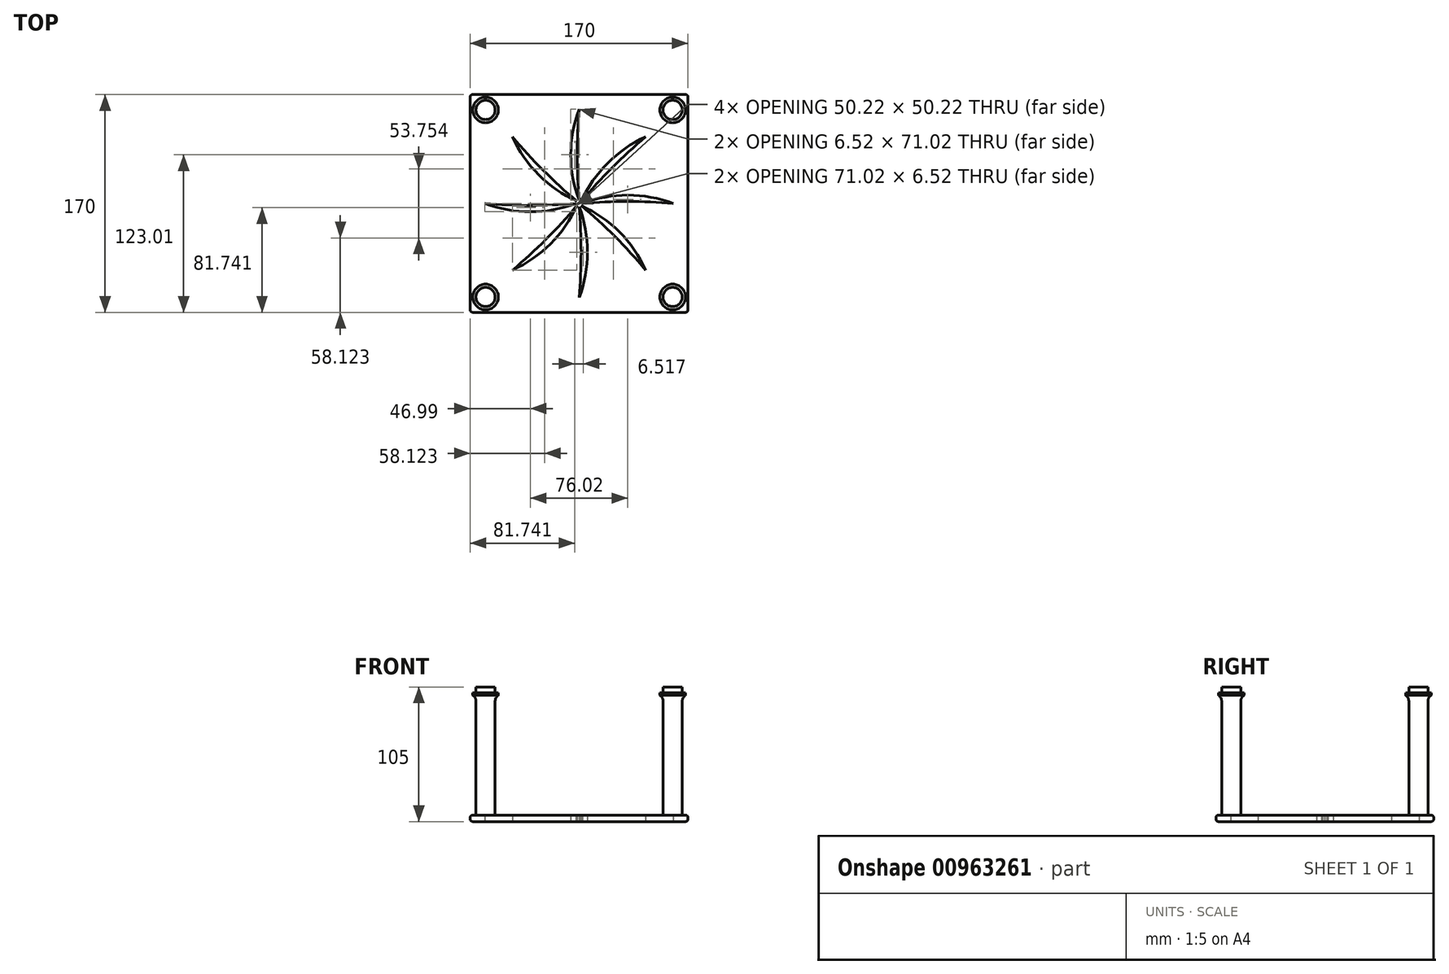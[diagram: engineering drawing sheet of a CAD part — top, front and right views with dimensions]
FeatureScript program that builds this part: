
annotation { "Feature Type Name" : "Feature", "Feature Type Description" : "" }
export const myFeature = defineFeature(function(context is Context, id is Id, definition is map)
    precondition{}
    {
        {
            var Q0;
            Q0=qCreatedBy(makeId("Top.planeOp"),FACE);
            var sketch = newSketch(context, id + "F0", { "sketchPlane" : qUnion([Q0])});
            skLineSegment(sketch, "E0.bottom", {"start": v(85, -85) * mm, "end": v(-85, -85) * mm});
            skLineSegment(sketch, "E0.top", {"start": v(85, 85) * mm, "end": v(-85, 85) * mm});
            skLineSegment(sketch, "E0.left", {"start": v(85, -85) * mm, "end": v(85, 85) * mm});
            skLineSegment(sketch, "E0.right", {"start": v(-85, -85) * mm, "end": v(-85, 85) * mm});
            skPoint(sketch, "E0.middle", {"position": v(0, 0) * mm});
            skSolve(sketch);
        }
        {
            var Q0;
            Q0 = qSketchRegion(id + "F0", true);
            extrude(context, id + "F1", {"entities" : qUnion([Q0]), "depth" : 5 * mm, "offsetDistance" : 25 * mm});
        }
        {
            var Q0;
            Q0=makeQuery(id+"F1.opExtrude","CAP_EDGE",EDGE,{"disambiguationData":[OSD([sQuery(id+"F0.wireOp",EDGE,"E0.bottom")])],"isStart":false});
            var Q1;
            Q1=makeQuery(id+"F1.opExtrude","CAP_EDGE",EDGE,{"disambiguationData":[OSD([sQuery(id+"F0.wireOp",EDGE,"E0.top")])],"isStart":true});
            var Q2;
            Q2=makeQuery(id+"F1.opExtrude","CAP_EDGE",EDGE,{"disambiguationData":[OSD([sQuery(id+"F0.wireOp",EDGE,"E0.top")])],"isStart":false});
            var Q3;
            Q3=makeQuery(id+"F1.opExtrude","CAP_EDGE",EDGE,{"disambiguationData":[OSD([sQuery(id+"F0.wireOp",EDGE,"E0.left")])],"isStart":false});
            var Q4;
            Q4=makeQuery(id+"F1.opExtrude","CAP_EDGE",EDGE,{"disambiguationData":[OSD([sQuery(id+"F0.wireOp",EDGE,"E0.right")])],"isStart":true});
            var Q5;
            Q5=makeQuery(id+"F1.opExtrude","CAP_EDGE",EDGE,{"disambiguationData":[OSD([sQuery(id+"F0.wireOp",EDGE,"E0.right")])],"isStart":false});
            var Q6;
            Q6=makeQuery(id+"F1.opExtrude","SWEPT_EDGE",EDGE,{"disambiguationData":[OSD([sQuery(id+"F0.wireOp",EDGE,"E0.bottom"),sQuery(id+"F0.wireOp",EDGE,"E0.left")])]});
            var Q7;
            Q7=makeQuery(id+"F1.opExtrude","SWEPT_EDGE",EDGE,{"disambiguationData":[OSD([sQuery(id+"F0.wireOp",EDGE,"E0.bottom"),sQuery(id+"F0.wireOp",EDGE,"E0.right")])]});
            var Q8;
            Q8=makeQuery(id+"F1.opExtrude","SWEPT_EDGE",EDGE,{"disambiguationData":[OSD([sQuery(id+"F0.wireOp",EDGE,"E0.top"),sQuery(id+"F0.wireOp",EDGE,"E0.left")])]});
            var Q9;
            Q9=makeQuery(id+"F1.opExtrude","SWEPT_EDGE",EDGE,{"disambiguationData":[OSD([sQuery(id+"F0.wireOp",EDGE,"E0.top"),sQuery(id+"F0.wireOp",EDGE,"E0.right")])]});
            var Q10;
            Q10=makeQuery(id+"F1.opExtrude","CAP_EDGE",EDGE,{"disambiguationData":[OSD([sQuery(id+"F0.wireOp",EDGE,"E0.bottom")])],"isStart":true});
            var Q11;
            Q11=makeQuery(id+"F1.opExtrude","CAP_EDGE",EDGE,{"disambiguationData":[OSD([sQuery(id+"F0.wireOp",EDGE,"E0.left")])],"isStart":true});
            fillet(context, id + "F2", {"entities" : qUnion([Q0, Q1, Q2, Q3, Q4, Q5, Q6, Q7, Q8, Q9, Q10, Q11]), "radius" : 2 * mm, "tangentPropagation" : true, "allowEdgeOverflow" : false});
        }
        {
            var Q0;
            Q0=makeQuery(id+"F1.opExtrude","CAP_FACE",FACE,{"disambiguationData":[OSD([sQuery(id+"F0.wireOp",EDGE,"E0.bottom"),sQuery(id+"F0.wireOp",EDGE,"E0.top"),sQuery(id+"F0.wireOp",EDGE,"E0.left"),sQuery(id+"F0.wireOp",EDGE,"E0.right")])],"isStart":false});
            var sketch = newSketch(context, id + "F3", { "sketchPlane" : qUnion([Q0])});
            skLineSegment(sketch, "E1", {"start": v(-83, 83) * mm, "end": v(-83, 73) * mm, "construction": true});
            skLineSegment(sketch, "E2", {"start": v(-83, 73) * mm, "end": v(-73, 73) * mm, "construction": true});
            skCircle(sketch, "E3", {"center": v(-73, 73) * mm, "radius": 7.5 * mm});
            skLineSegment(sketch, "E4", {"start": v(83, 83) * mm, "end": v(83, 73) * mm, "construction": true});
            skLineSegment(sketch, "E5", {"start": v(83, 73) * mm, "end": v(73, 73) * mm, "construction": true});
            skCircle(sketch, "E6", {"center": v(73, 73) * mm, "radius": 7.5 * mm});
            skLineSegment(sketch, "E7", {"start": v(83, -83) * mm, "end": v(83, -73) * mm, "construction": true});
            skLineSegment(sketch, "E8", {"start": v(83, -73) * mm, "end": v(73, -73) * mm, "construction": true});
            skCircle(sketch, "E9", {"center": v(73, -73) * mm, "radius": 7.5 * mm});
            skLineSegment(sketch, "E10", {"start": v(-83, -83) * mm, "end": v(-73, -83) * mm, "construction": true});
            skLineSegment(sketch, "E11", {"start": v(-73, -83) * mm, "end": v(-73, -73) * mm, "construction": true});
            skCircle(sketch, "E12", {"center": v(-73, -73) * mm, "radius": 7.5 * mm});
            skSolve(sketch);
        }
        {
            var Q0;
            Q0 = qSketchRegion(id + "F3", true);
            extrude(context, id + "F4", {"entities" : qUnion([Q0]), "operationType" : NewBodyOperationType.ADD, "depth" : 95.5 * mm, "offsetDistance" : 25 * mm});
        }
        {
            var Q0;
            Q0=makeQuery(id+"F4.opExtrude","CAP_FACE",FACE,{"disambiguationData":[OSD([sQuery(id+"F3.wireOp",EDGE,"E3")])],"isStart":false});
            var sketch = newSketch(context, id + "F5", { "sketchPlane" : qUnion([Q0])});
            skCircle(sketch, "E13", {"center": v(-73, 73) * mm, "radius": 10 * mm});
            skSolve(sketch);
        }
        {
            var Q0;
            Q0=makeQuery(id+"F4.opExtrude","CAP_FACE",FACE,{"disambiguationData":[OSD([sQuery(id+"F3.wireOp",EDGE,"E6")])],"isStart":false});
            var sketch = newSketch(context, id + "F6", { "sketchPlane" : qUnion([Q0])});
            skCircle(sketch, "E14", {"center": v(73, 73) * mm, "radius": 10 * mm});
            skSolve(sketch);
        }
        {
            var Q0;
            Q0=makeQuery(id+"F4.opExtrude","CAP_FACE",FACE,{"disambiguationData":[OSD([sQuery(id+"F3.wireOp",EDGE,"E9")])],"isStart":false});
            var sketch = newSketch(context, id + "F7", { "sketchPlane" : qUnion([Q0])});
            skCircle(sketch, "E15", {"center": v(73, -73) * mm, "radius": 10 * mm});
            skSolve(sketch);
        }
        {
            var Q0;
            Q0=makeQuery(id+"F4.opExtrude","CAP_FACE",FACE,{"disambiguationData":[OSD([sQuery(id+"F3.wireOp",EDGE,"E12")])],"isStart":false});
            var sketch = newSketch(context, id + "F8", { "sketchPlane" : qUnion([Q0])});
            skCircle(sketch, "E16", {"center": v(-73, -73) * mm, "radius": 10 * mm});
            skSolve(sketch);
        }
        {
            var Q0;
            Q0=makeQuery(id+"F5.imprint","IMPRINT",FACE,{"disambiguationData":[TD([[makeQuery(id+"F5.imprint","IMPRINT",EDGE,{"derivedFrom":makeQuery(id+"F4.opExtrude","CAP_EDGE",EDGE,{"disambiguationData":[OSD([sQuery(id+"F3.wireOp",EDGE,"E3")])],"isStart":false})}),1.0]])]});
            var Q1;
            Q1=makeQuery(id+"F6.imprint","IMPRINT",FACE,{"disambiguationData":[TD([[makeQuery(id+"F6.imprint","IMPRINT",EDGE,{"derivedFrom":makeQuery(id+"F4.opExtrude","CAP_EDGE",EDGE,{"disambiguationData":[OSD([sQuery(id+"F3.wireOp",EDGE,"E6")])],"isStart":false})}),1.0]])]});
            var Q2;
            Q2=makeQuery(id+"F7.imprint","IMPRINT",FACE,{"disambiguationData":[TD([[makeQuery(id+"F7.imprint","IMPRINT",EDGE,{"derivedFrom":makeQuery(id+"F4.opExtrude","CAP_EDGE",EDGE,{"disambiguationData":[OSD([sQuery(id+"F3.wireOp",EDGE,"E9")])],"isStart":false})}),1.0]])]});
            var Q3;
            Q3=makeQuery(id+"F8.imprint","IMPRINT",FACE,{"disambiguationData":[TD([[makeQuery(id+"F8.imprint","IMPRINT",EDGE,{"derivedFrom":makeQuery(id+"F4.opExtrude","CAP_EDGE",EDGE,{"disambiguationData":[OSD([sQuery(id+"F3.wireOp",EDGE,"E12")])],"isStart":false})}),1.0]])]});
            extrude(context, id + "F9", {"entities" : qUnion([Q0, Q1, Q2, Q3]), "operationType" : NewBodyOperationType.ADD, "depth" : 4.5 * mm, "offsetDistance" : 25 * mm});
        }
        {
            var Q0;
            Q0=makeQuery(id+"F5.imprint","IMPRINT",FACE,{"disambiguationData":[TD([[makeQuery(id+"F5.imprint","IMPRINT",EDGE,{"derivedFrom":sQuery(id+"F5.wireOp",EDGE,"E13")}),1.0]])]});
            var Q1;
            Q1=makeQuery(id+"F6.imprint","IMPRINT",FACE,{"disambiguationData":[TD([[makeQuery(id+"F6.imprint","IMPRINT",EDGE,{"derivedFrom":sQuery(id+"F6.wireOp",EDGE,"E14")}),1.0]])]});
            var Q2;
            Q2=makeQuery(id+"F7.imprint","IMPRINT",FACE,{"disambiguationData":[TD([[makeQuery(id+"F7.imprint","IMPRINT",EDGE,{"derivedFrom":sQuery(id+"F7.wireOp",EDGE,"E15")}),1.0]])]});
            var Q3;
            Q3=makeQuery(id+"F8.imprint","IMPRINT",FACE,{"disambiguationData":[TD([[makeQuery(id+"F8.imprint","IMPRINT",EDGE,{"derivedFrom":sQuery(id+"F8.wireOp",EDGE,"E16")}),1.0]])]});
            extrude(context, id + "F10", {"entities" : qUnion([Q0, Q1, Q2, Q3]), "operationType" : NewBodyOperationType.ADD, "oppositeDirection" : true, "depth" : 2 * mm, "offsetDistance" : 25 * mm});
        }
        {
            var Q0;
            Q0=makeQuery(id+"F1.opExtrude","CAP_FACE",FACE,{"disambiguationData":[OSD([sQuery(id+"F0.wireOp",EDGE,"E0.bottom"),sQuery(id+"F0.wireOp",EDGE,"E0.top"),sQuery(id+"F0.wireOp",EDGE,"E0.left"),sQuery(id+"F0.wireOp",EDGE,"E0.right")])],"isStart":true});
            var sketch = newSketch(context, id + "F11", { "sketchPlane" : qUnion([Q0])});
            skCircle(sketch, "E17", {"center": v(0, 0) * mm, "radius": 25 * mm});
            skCircle(sketch, "E18", {"center": v(0, 0) * mm, "radius": 2.5 * mm});
            skArc(sketch, "E19", {"start": v(-2.5, 0) * mm, "mid": v(-38, 6.52) * mm, "end": v(-73.52, 0) * mm});
            skArc(sketch, "E20", {"start": v(-2.5, 0) * mm, "mid": v(-38, 1.52) * mm, "end": v(-73.52, 0) * mm});
            skSolve(sketch);
        }
        {
            var Q0;
            {var subQ0=sQuery(id+"F11.wireOp",EDGE,"xrmHhvh0-mqmk-Dxvq-12wP-874APo94u9yt");var subQ1=sQuery(id+"F11.wireOp",EDGE,"E17");var subQ2=makeQuery(id+"F11.imprint","INTERSECT",VERTEX,{"derivedFrom":[subQ1,subQ0]});Q0=makeQuery(id+"F11.imprint","IMPRINT",FACE,{"disambiguationData":[TD([[makeQuery(id+"F11.imprint","IMPRINT",EDGE,{"disambiguationData":[TD([[subQ2,1.0]])],"derivedFrom":subQ1}),-1.0]])]});}
            var Q1;
            {var subQ0=sQuery(id+"F11.wireOp",EDGE,"3R2oN2jj-0wEl-wqH8-dfdT-mFaKYkVUSXbc");var subQ1=sQuery(id+"F11.wireOp",EDGE,"E17");var subQ2=makeQuery(id+"F11.imprint","INTERSECT",VERTEX,{"derivedFrom":[subQ1,subQ0]});Q1=makeQuery(id+"F11.imprint","IMPRINT",FACE,{"disambiguationData":[TD([[makeQuery(id+"F11.imprint","IMPRINT",EDGE,{"disambiguationData":[TD([[subQ2,-1.0]])],"derivedFrom":subQ1}),1.0]])]});}
            extrude(context, id + "F12", {"entities" : qUnion([Q0, Q1]), "depth" : 25 * mm, "offsetDistance" : 25 * mm});
        }
        {
            var Q0;
            Q0=makeQuery(id+"F12.opExtrude","SWEPT_BODY",BODY,{"disambiguationData":[OSD([sQuery(id+"F11.wireOp",EDGE,"E19"),sQuery(id+"F11.wireOp",EDGE,"E20")])]});
            var Q1;
            Q1=sQuery(id+"F11.wireOp",EDGE,"E17");
            circularPattern(context, id + "F13", {"entities" : qUnion([Q0]), "axis" : qUnion([Q1]), "angle" : 360 * degree, "instanceCount" : 8, "equalSpace" : true});
        }
        {
            var Q0;
            Q0=makeQuery(id+"F13.opPattern","COPY",FACE,{"derivedFrom":makeQuery(id+"F12.opExtrude","CAP_FACE",FACE,{"disambiguationData":[OSD([sQuery(id+"F11.wireOp",EDGE,"E19"),sQuery(id+"F11.wireOp",EDGE,"E20")])],"isStart":false}),"instanceName":"6"});
            var Q1;
            Q1=makeQuery(id+"F13.opPattern","COPY",FACE,{"derivedFrom":makeQuery(id+"F12.opExtrude","CAP_FACE",FACE,{"disambiguationData":[OSD([sQuery(id+"F11.wireOp",EDGE,"E19"),sQuery(id+"F11.wireOp",EDGE,"E20")])],"isStart":false}),"instanceName":"7"});
            var Q2;
            Q2=makeQuery(id+"F13.opPattern","COPY",FACE,{"derivedFrom":makeQuery(id+"F12.opExtrude","CAP_FACE",FACE,{"disambiguationData":[OSD([sQuery(id+"F11.wireOp",EDGE,"E19"),sQuery(id+"F11.wireOp",EDGE,"E20")])],"isStart":false}),"instanceName":"5"});
            var Q3;
            Q3=makeQuery(id+"F13.opPattern","COPY",FACE,{"derivedFrom":makeQuery(id+"F12.opExtrude","CAP_FACE",FACE,{"disambiguationData":[OSD([sQuery(id+"F11.wireOp",EDGE,"E19"),sQuery(id+"F11.wireOp",EDGE,"E20")])],"isStart":false}),"instanceName":"4"});
            var Q4;
            Q4=makeQuery(id+"F13.opPattern","COPY",FACE,{"derivedFrom":makeQuery(id+"F12.opExtrude","CAP_FACE",FACE,{"disambiguationData":[OSD([sQuery(id+"F11.wireOp",EDGE,"E19"),sQuery(id+"F11.wireOp",EDGE,"E20")])],"isStart":false}),"instanceName":"3"});
            var Q5;
            Q5=makeQuery(id+"F13.opPattern","COPY",FACE,{"derivedFrom":makeQuery(id+"F12.opExtrude","CAP_FACE",FACE,{"disambiguationData":[OSD([sQuery(id+"F11.wireOp",EDGE,"E19"),sQuery(id+"F11.wireOp",EDGE,"E20")])],"isStart":false}),"instanceName":"2"});
            var Q6;
            Q6=makeQuery(id+"F13.opPattern","COPY",FACE,{"derivedFrom":makeQuery(id+"F12.opExtrude","CAP_FACE",FACE,{"disambiguationData":[OSD([sQuery(id+"F11.wireOp",EDGE,"E19"),sQuery(id+"F11.wireOp",EDGE,"E20")])],"isStart":false}),"instanceName":"1"});
            var Q7;
            Q7=makeQuery(id+"F12.opExtrude","CAP_FACE",FACE,{"disambiguationData":[OSD([sQuery(id+"F11.wireOp",EDGE,"E19"),sQuery(id+"F11.wireOp",EDGE,"E20")])],"isStart":false});
            extrude(context, id + "F14", {"entities" : qUnion([Q0, Q1, Q2, Q3, Q4, Q5, Q6, Q7]), "operationType" : NewBodyOperationType.REMOVE, "oppositeDirection" : true, "depth" : 50 * mm, "offsetDistance" : 25 * mm});
        }
        {
            var Q0;
            Q0=makeQuery(id+"F10.opExtrude","CAP_EDGE",EDGE,{"disambiguationData":[OSD([sQuery(id+"F3.wireOp",EDGE,"E12")])],"isStart":false});
            var Q1;
            Q1=makeQuery(id+"F10.opExtrude","CAP_EDGE",EDGE,{"disambiguationData":[OSD([sQuery(id+"F3.wireOp",EDGE,"E6")])],"isStart":false});
            var Q2;
            Q2=makeQuery(id+"F10.opExtrude","CAP_EDGE",EDGE,{"disambiguationData":[OSD([sQuery(id+"F3.wireOp",EDGE,"E3")])],"isStart":false});
            var Q3;
            Q3=makeQuery(id+"F10.opExtrude","CAP_EDGE",EDGE,{"disambiguationData":[OSD([sQuery(id+"F3.wireOp",EDGE,"E9")])],"isStart":false});
            fillet(context, id + "F15", {"entities" : qUnion([Q0, Q1, Q2, Q3]), "radius" : 5 * mm, "tangentPropagation" : true, "allowEdgeOverflow" : false});
        }
    });
